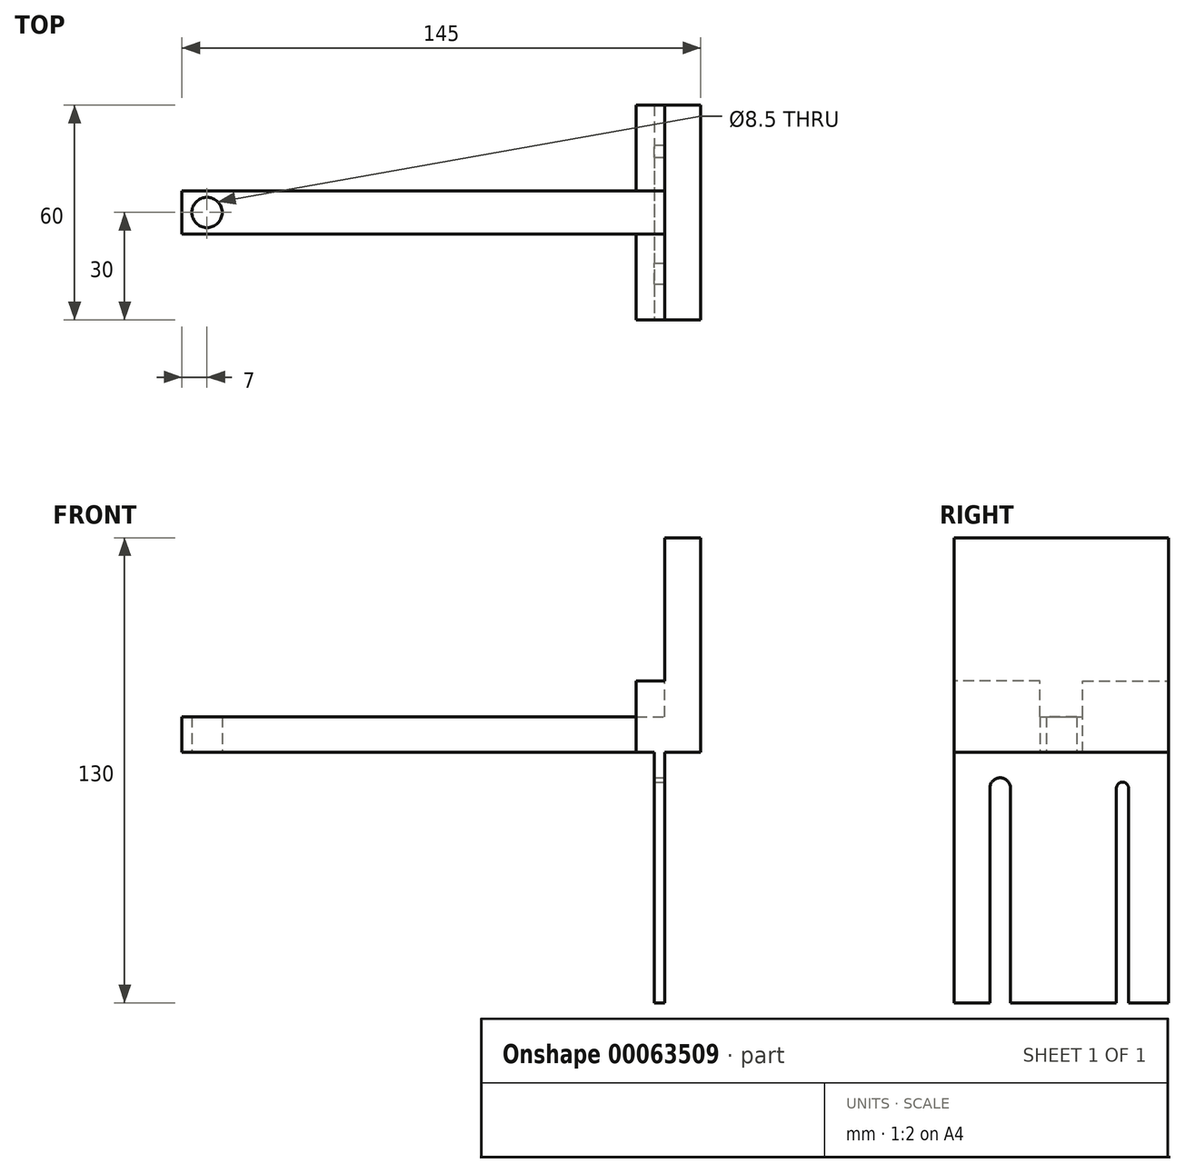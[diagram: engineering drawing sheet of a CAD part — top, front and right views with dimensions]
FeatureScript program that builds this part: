
annotation { "Feature Type Name" : "Feature", "Feature Type Description" : "" }
export const myFeature = defineFeature(function(context is Context, id is Id, definition is map)
    precondition{}
    {
        {
            var Q0;
            Q0=qCreatedBy(makeId("Top.planeOp"),FACE);
            var sketch = newSketch(context, id + "F0", { "sketchPlane" : qUnion([Q0])});
            skLineSegment(sketch, "E0.bottom", {"start": v(-70, 6) * mm, "end": v(70, 6) * mm});
            skLineSegment(sketch, "E0.top", {"start": v(-70, -6) * mm, "end": v(70, -6) * mm});
            skLineSegment(sketch, "E0.left", {"start": v(-70, 6) * mm, "end": v(-70, -6) * mm});
            skLineSegment(sketch, "E0.right", {"start": v(70, 6) * mm, "end": v(70, -6) * mm});
            skLineSegment(sketch, "E1", {"start": v(-70, 6) * mm, "end": v(70, -6) * mm, "construction": true});
            skLineSegment(sketch, "E2", {"start": v(-70, -6) * mm, "end": v(70, 6) * mm, "construction": true});
            skPoint(sketch, "E3", {"position": v(0, 0) * mm});
            skLineSegment(sketch, "E4", {"start": v(-70, 0) * mm, "end": v(70, 0) * mm, "construction": true});
            skLineSegment(sketch, "E5.rect.bottom", {"start": v(75, -30) * mm, "end": v(65, -30) * mm});
            skLineSegment(sketch, "E5.rect.top", {"start": v(75, 30) * mm, "end": v(65, 30) * mm});
            skLineSegment(sketch, "E5.rect.left", {"start": v(75, -30) * mm, "end": v(75, 30) * mm});
            skLineSegment(sketch, "E5.rect.right", {"start": v(65, -30) * mm, "end": v(65, 30) * mm});
            skPoint(sketch, "E5.rect.middle", {"position": v(70, 0) * mm});
            skCircle(sketch, "E6", {"center": v(-63, 0) * mm, "radius": 4.25 * mm});
            skSolve(sketch);
        }
        {
            var Q0;
            {var subQ0=sQuery(id+"F0.wireOp",EDGE,"E0.left");Q0=makeQuery(id+"F0.imprint","IMPRINT",FACE,{"disambiguationData":[TD([[makeQuery(id+"F0.imprint","IMPRINT",EDGE,{"derivedFrom":subQ0}),1.0]])]});}
            extrude(context, id + "F1", {"entities" : qUnion([Q0]), "depth" : 10 * mm});
        }
        {
            var Q0;
            {var subQ1=sQuery(id+"F0.wireOp",EDGE,"E0.right");Q0=makeQuery(id+"F0.imprint","IMPRINT",FACE,{"disambiguationData":[TD([[makeQuery(id+"F0.imprint","IMPRINT",EDGE,{"derivedFrom":subQ1}),1.0]])]});}
            var Q1;
            {var subQ0=sQuery(id+"F0.wireOp",EDGE,"E0.right");Q1=makeQuery(id+"F0.imprint","IMPRINT",FACE,{"disambiguationData":[TD([[makeQuery(id+"F0.imprint","IMPRINT",EDGE,{"derivedFrom":subQ0}),-1.0]])]});}
            extrude(context, id + "F2", {"entities" : qUnion([Q0, Q1]), "operationType" : NewBodyOperationType.ADD, "depth" : 60 * mm});
        }
        {
            var Q0;
            Q0=makeQuery(id+"F2.opExtrude","SWEPT_FACE",FACE,{"disambiguationData":[OSD([sQuery(id+"F0.wireOp",EDGE,"E5.rect.right")])]});
            var sketch = newSketch(context, id + "F3", { "sketchPlane" : qUnion([Q0])});
            skLineSegment(sketch, "E7.bottom", {"start": v(-30, 0) * mm, "end": v(30, 0) * mm});
            skLineSegment(sketch, "E7.top", {"start": v(-30, -70) * mm, "end": v(30, -70) * mm});
            skLineSegment(sketch, "E7.left", {"start": v(-30, 0) * mm, "end": v(-30, -70) * mm});
            skLineSegment(sketch, "E7.right", {"start": v(30, 0) * mm, "end": v(30, -70) * mm});
            skLineSegment(sketch, "E8.bottom", {"start": v(6, 0) * mm, "end": v(30, 0) * mm});
            skLineSegment(sketch, "E8.top", {"start": v(6, 20) * mm, "end": v(30, 20) * mm});
            skLineSegment(sketch, "E8.left", {"start": v(6, 0) * mm, "end": v(6, 20) * mm});
            skLineSegment(sketch, "E8.right", {"start": v(30, 0) * mm, "end": v(30, 20) * mm});
            skLineSegment(sketch, "E9.bottom", {"start": v(-6, 0) * mm, "end": v(-30, 0) * mm});
            skLineSegment(sketch, "E9.top", {"start": v(-6, 20) * mm, "end": v(-30, 20) * mm});
            skLineSegment(sketch, "E9.left", {"start": v(-6, 0) * mm, "end": v(-6, 20) * mm});
            skLineSegment(sketch, "E9.right", {"start": v(-30, 0) * mm, "end": v(-30, 20) * mm});
            skLineSegment(sketch, "E10", {"start": v(-18.8, -70) * mm, "end": v(-18.8, -10) * mm});
            skLineSegment(sketch, "E11.0", {"start": v(-15.4, -70) * mm, "end": v(-15.4, -10) * mm});
            skArc(sketch, "E12", {"start": v(-15.4, -10) * mm, "mid": v(-17.1, -8.3) * mm, "end": v(-18.8, -10) * mm});
            skLineSegment(sketch, "E13.0", {"start": v(-20, -70) * mm, "end": v(-20, -10) * mm});
            skArc(sketch, "E13.1", {"start": v(-14.2, -10) * mm, "mid": v(-17.1, -7.1) * mm, "end": v(-20, -10) * mm});
            skLineSegment(sketch, "E13.2", {"start": v(-14.2, -70) * mm, "end": v(-14.2, -10) * mm});
            skArc(sketch, "E14.MirrorCS", {"start": v(14.2, -10) * mm, "mid": v(17.1, -7.1) * mm, "end": v(20, -10) * mm});
            skLineSegment(sketch, "E15.MirrorCS", {"start": v(14.2, -70) * mm, "end": v(14.2, -10) * mm});
            skLineSegment(sketch, "E16.MirrorCS", {"start": v(18.8, -70) * mm, "end": v(18.8, -10) * mm});
            skArc(sketch, "E17.MirrorCS", {"start": v(15.4, -10) * mm, "mid": v(17.1, -8.3) * mm, "end": v(18.8, -10) * mm});
            skLineSegment(sketch, "E18.MirrorCS", {"start": v(20, -70) * mm, "end": v(20, -10) * mm});
            skLineSegment(sketch, "E19.MirrorCS", {"start": v(15.4, -70) * mm, "end": v(15.4, -10) * mm});
            skSolve(sketch);
        }
        {
            var Q0;
            Q0=makeQuery(id+"F3.imprint","IMPRINT",FACE,{"disambiguationData":[TD([[makeQuery(id+"F3.imprint","IMPRINT",EDGE,{"derivedFrom":sQuery(id+"F3.wireOp",EDGE,"E7.bottom")}),-1.0]])]});
            var Q1;
            {var subQ3=sQuery(id+"F3.wireOp",EDGE,"E9.bottom");Q1=makeQuery(id+"F3.imprint","IMPRINT",FACE,{"disambiguationData":[TD([[makeQuery(id+"F3.imprint","IMPRINT",EDGE,{"derivedFrom":subQ3}),-1.0]])]});}
            var Q2;
            {var subQ3=sQuery(id+"F3.wireOp",EDGE,"E8.bottom");Q2=makeQuery(id+"F3.imprint","IMPRINT",FACE,{"disambiguationData":[TD([[makeQuery(id+"F3.imprint","IMPRINT",EDGE,{"derivedFrom":subQ3}),-1.0]])]});}
            extrude(context, id + "F4", {"entities" : qUnion([Q0, Q1, Q2]), "depth" : 5 * mm});
        }
        {
            var Q0;
            {var subQ1=sQuery(id+"F3.wireOp",EDGE,"E10");Q0=makeQuery(id+"F3.imprint","IMPRINT",FACE,{"disambiguationData":[TD([[makeQuery(id+"F3.imprint","IMPRINT",EDGE,{"derivedFrom":subQ1}),1.0]])]});}
            var Q1;
            Q1=makeQuery(id+"F3.imprint","IMPRINT",FACE,{"disambiguationData":[TD([[makeQuery(id+"F3.imprint","IMPRINT",EDGE,{"derivedFrom":sQuery(id+"F3.wireOp",EDGE,"E14.MirrorCS")}),-1.0]])]});
            var Q2;
            Q2=makeQuery(id+"F4.opExtrude","CAP_FACE",FACE,{"disambiguationData":[OSD([sQuery(id+"F3.wireOp",EDGE,"E7.bottom"),sQuery(id+"F3.wireOp",EDGE,"E7.top"),sQuery(id+"F3.wireOp",EDGE,"E7.left"),sQuery(id+"F3.wireOp",EDGE,"E7.right"),sQuery(id+"F3.wireOp",EDGE,"E8.top"),sQuery(id+"F3.wireOp",EDGE,"E8.left"),sQuery(id+"F3.wireOp",EDGE,"E8.right"),sQuery(id+"F3.wireOp",EDGE,"E9.top"),sQuery(id+"F3.wireOp",EDGE,"E9.left"),sQuery(id+"F3.wireOp",EDGE,"E9.right"),sQuery(id+"F3.wireOp",EDGE,"E13.0"),sQuery(id+"F3.wireOp",EDGE,"E13.1"),sQuery(id+"F3.wireOp",EDGE,"E13.2"),sQuery(id+"F3.wireOp",EDGE,"E14.MirrorCS"),sQuery(id+"F3.wireOp",EDGE,"E15.MirrorCS"),sQuery(id+"F3.wireOp",EDGE,"E18.MirrorCS")])],"isStart":false});
            var Q3;
            Q3=makeQuery(id+"F3.imprint","IMPRINT",FACE,{"disambiguationData":[TD([[makeQuery(id+"F3.imprint","IMPRINT",EDGE,{"derivedFrom":sQuery(id+"F3.wireOp",EDGE,"E7.bottom")}),-1.0]])]});
            var Q4;
            Q4=makeQuery(id+"F4.opExtrude","CAP_FACE",FACE,{"disambiguationData":[OSD([sQuery(id+"F3.wireOp",EDGE,"E7.bottom"),sQuery(id+"F3.wireOp",EDGE,"E7.top"),sQuery(id+"F3.wireOp",EDGE,"E7.left"),sQuery(id+"F3.wireOp",EDGE,"E7.right"),sQuery(id+"F3.wireOp",EDGE,"E8.top"),sQuery(id+"F3.wireOp",EDGE,"E8.left"),sQuery(id+"F3.wireOp",EDGE,"E8.right"),sQuery(id+"F3.wireOp",EDGE,"E9.top"),sQuery(id+"F3.wireOp",EDGE,"E9.left"),sQuery(id+"F3.wireOp",EDGE,"E9.right"),sQuery(id+"F3.wireOp",EDGE,"E13.0"),sQuery(id+"F3.wireOp",EDGE,"E13.1"),sQuery(id+"F3.wireOp",EDGE,"E13.2"),sQuery(id+"F3.wireOp",EDGE,"E14.MirrorCS"),sQuery(id+"F3.wireOp",EDGE,"E15.MirrorCS"),sQuery(id+"F3.wireOp",EDGE,"E18.MirrorCS")])],"isStart":true});
            extrude(context, id + "F5", {"entities" : qUnion([Q0, Q1, Q2, Q3, Q4]), "operationType" : NewBodyOperationType.ADD, "depth" : 3 * mm});
        }
    });
